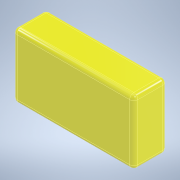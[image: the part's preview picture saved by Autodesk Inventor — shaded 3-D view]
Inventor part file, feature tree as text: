
AUTODESK INVENTOR PART (.ipt)
format: ipt  version: 2021 (Build 250183000, 183)  size: 117,248 bytes
history: native  units: mm
features: other x1, extrude x1, fillet x1, sketch x1
ambient origin geometry x8: Origin, YZ Plane, XZ Plane, XY Plane, X Axis, Y Axis, Z Axis, Center Point
bodies: Body1 (feature_tree)
feature tree (4):
  other  "Sólido1"
  extrude  "Extrusão1"  Depth=16.0mm
  fillet  "Arredondamento1"  Radius=31.0mm
  sketch  "Esboço1"  dims[d0=58.0mm d1=16.0mm d2=31.0mm d3=0.0mm d4=2.0mm]
